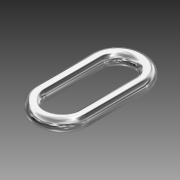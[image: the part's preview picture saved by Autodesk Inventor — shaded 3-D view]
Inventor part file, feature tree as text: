
AUTODESK INVENTOR PART (.ipt)
format: ipt  version: 2013 (Build 170138000, 138)  size: 135,680 bytes
history: native  units: mm (DEFAULTED — no unit token found)
features: other x7, sketch x5, plane x2, sweep x1
ambient origin geometry x8: Origin, YZ Plane, XZ Plane, XY Plane, X Axis, Y Axis, Z Axis, Center Point
bodies: Solid1 (feature_tree)
feature tree (15):
  sweep  "Sweep1"
  sketch  "Sketch3"  dims[d4=38.1mm]
  other  "Work Axis1"
  other  "Work Axis2"
  other  "Work Axis3"
  other  "Work Point1"
  other  "Work Point2"
  plane  "Work Plane1"
  sketch  "Sketch4"
  plane  "Work Plane2"
  sketch  "Sketch5"
  other  "Work Axis4"
  other  "Work Axis5"
  sketch  "Sketch1"  dims[d0=5.08mm d1=16.51mm]
  sketch  "Sketch2"  dims[d3=0.0mm]
